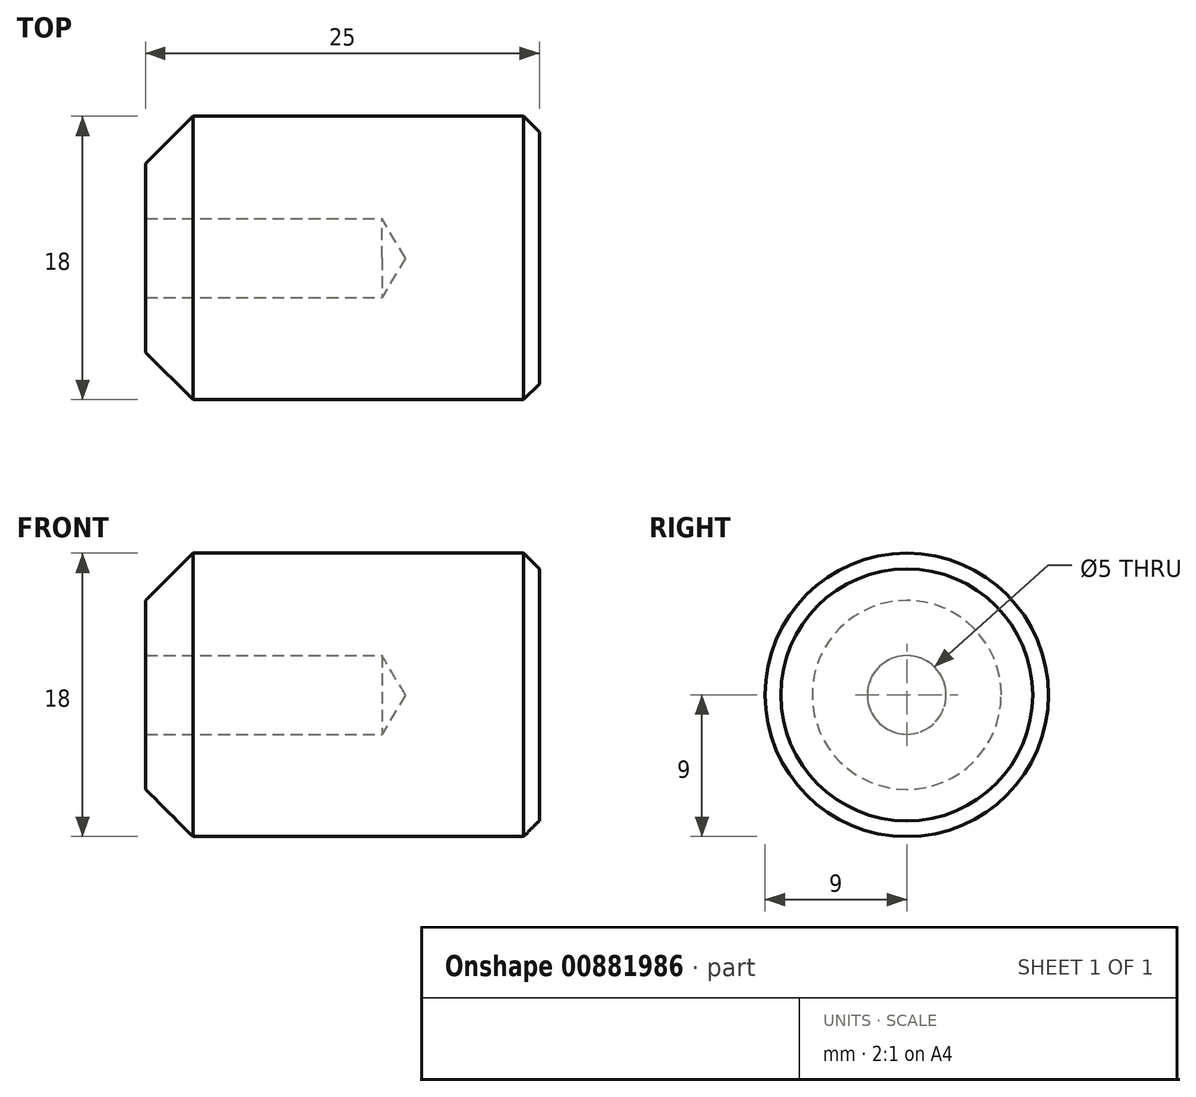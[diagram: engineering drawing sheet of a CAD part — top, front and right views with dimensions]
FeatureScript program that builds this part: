
annotation { "Feature Type Name" : "Feature", "Feature Type Description" : "" }
export const myFeature = defineFeature(function(context is Context, id is Id, definition is map)
    precondition{}
    {
        {
            var Q0;
            Q0=qCreatedBy(makeId("Front.planeOp"),FACE);
            var sketch = newSketch(context, id + "F0", { "sketchPlane" : qUnion([Q0])});
            skLineSegment(sketch, "E0.bottom", {"start": v(0, 0) * mm, "end": v(-25, 0) * mm});
            skLineSegment(sketch, "E0.left", {"start": v(0, 0) * mm, "end": v(0, 9) * mm});
            skLineSegment(sketch, "E1.top", {"start": v(0, 9) * mm, "end": v(-25, 9) * mm});
            skLineSegment(sketch, "E1.right", {"start": v(-25, 0) * mm, "end": v(-25, 9) * mm});
            skLineSegment(sketch, "E2", {"start": v(0, 0) * mm, "end": v(-25, 0) * mm, "construction": true});
            skLineSegment(sketch, "E3.trimOffspring", {"start": v(0, 0) * mm, "end": v(-40.86, 0) * mm, "construction": true});
            skSolve(sketch);
        }
        {
            var Q0;
            Q0=qSketchRegion(id+"F0",true);
            var Q1;
            Q1=sQuery(id+"F0.wireOp",EDGE,"E2");
            revolve(context, id + "F1", {"surfaceOperationType" : NewSurfaceOperationType.NEW, "entities" : qUnion([Q0]), "axis" : qUnion([Q1]), "revolveType" : RevolveType.FULL});
        }
        {
            var Q0;
            Q0=makeQuery(id+"F1.opRevolve","SWEPT_EDGE",EDGE,{"disambiguationData":[OSD([sQuery(id+"F0.wireOp",EDGE,"E0.left"),sQuery(id+"F0.wireOp",EDGE,"E1.top")])]});
            chamfer(context, id + "F2", {"entities" : qUnion([Q0]), "width" : 1 * mm, "tangentPropagation" : true});
        }
        {
            var Q0;
            Q0=makeQuery(id+"F1.opRevolve","SWEPT_EDGE",EDGE,{"disambiguationData":[OSD([sQuery(id+"F0.wireOp",EDGE,"E1.top"),sQuery(id+"F0.wireOp",EDGE,"E1.right")])]});
            chamfer(context, id + "F3", {"entities" : qUnion([Q0]), "width" : 3 * mm, "tangentPropagation" : true});
        }
        {
            var Q0;
            Q0=makeQuery(id+"F1.opRevolve","SWEPT_FACE",FACE,{"disambiguationData":[OSD([sQuery(id+"F0.wireOp",EDGE,"E1.right")])]});
            var sketch = newSketch(context, id + "F4", { "sketchPlane" : qUnion([Q0])});
            skPoint(sketch, "E4", {"position": v(0, 0) * mm});
            skSolve(sketch);
        }
        {
            var Q0;
            Q0=sQuery(id+"F4.wireOp",VERTEX,"E4");
            var Q1;
            Q1=makeQuery(id+"F1.opRevolve","SWEPT_BODY",BODY,{"disambiguationData":[OSD([sQuery(id+"F0.wireOp",EDGE,"E0.bottom"),sQuery(id+"F0.wireOp",EDGE,"E0.left"),sQuery(id+"F0.wireOp",EDGE,"E1.top"),sQuery(id+"F0.wireOp",EDGE,"E1.right")])]});
            hole(context, id + "F5", {"style" : HoleStyle.SIMPLE, "endStyle" : HoleEndStyle.BLIND, "standardTappedOrClearance" : lookupTablePath({ "standard" : "ISO", "engagement" : "75%", "pitch" : "1 mm", "size" : "M6", "type" : "Tapped" }), "standardBlindInLast" : lookupTablePath({ "standard" : "ISO", "engagement" : "75%", "pitch" : "1 mm", "size" : "M6", "type" : "Tapped" }), "holeDiameter" : 5 * mm, "majorDiameter" : 6 * mm, "showTappedDepth" : true, "holeDepth" : 15 * mm, "isTappedThrough" : true, "tappedDepth" : 12 * mm, "tapClearance" : 3, "locations" : qUnion([Q0]), "scope" : qUnion([Q1]), "startStyle" : HoleStartStyle.SKETCH});
        }
    });
